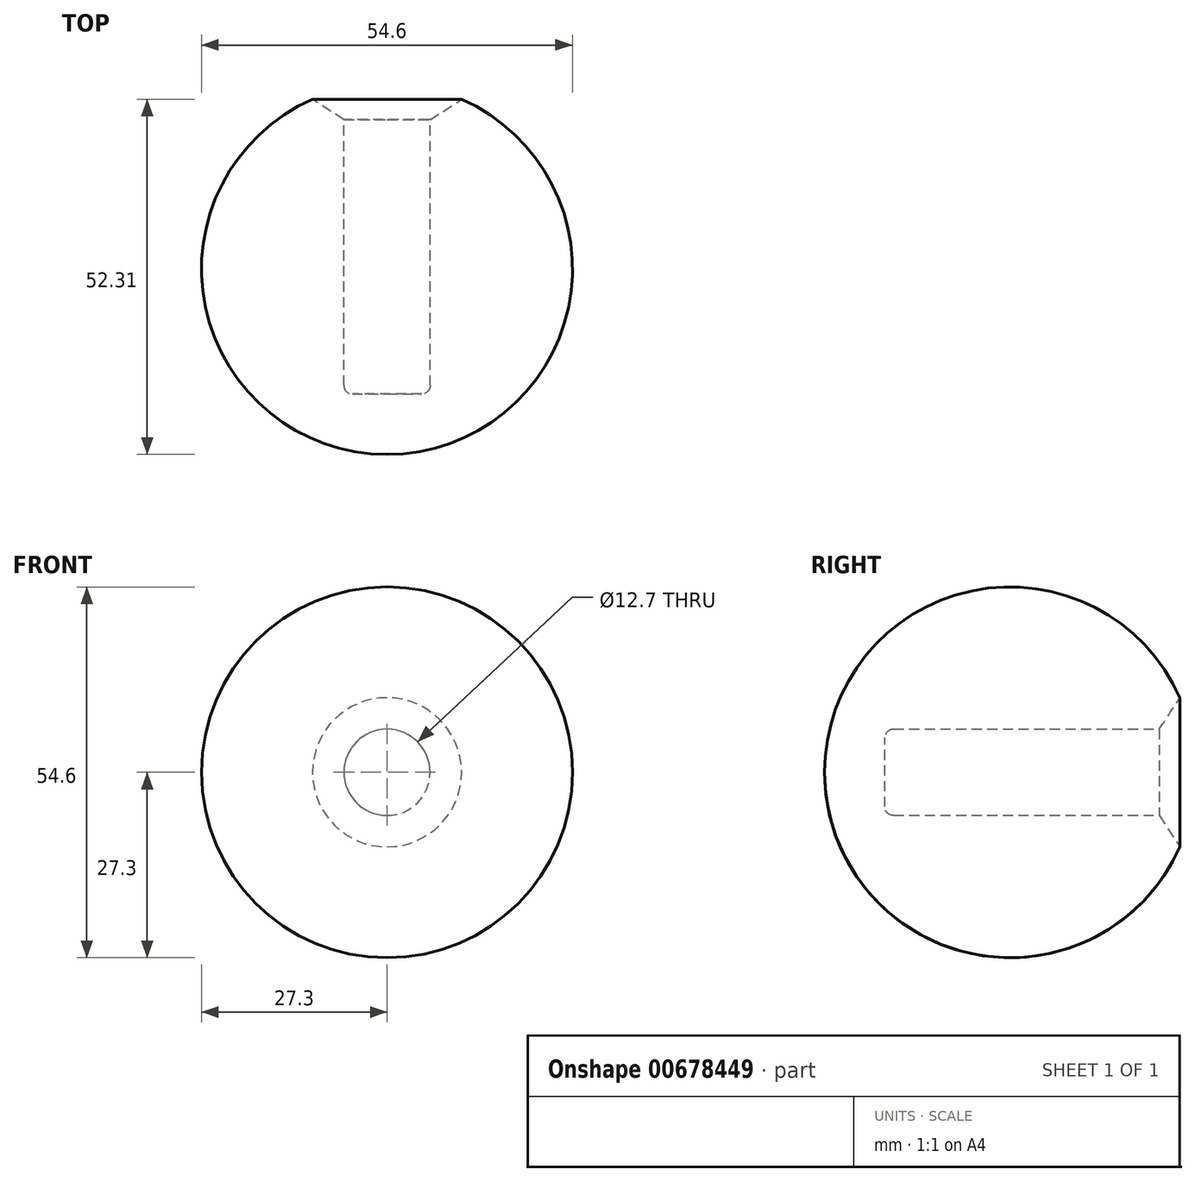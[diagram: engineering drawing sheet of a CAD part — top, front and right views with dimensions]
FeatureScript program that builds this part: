
annotation { "Feature Type Name" : "Feature", "Feature Type Description" : "" }
export const myFeature = defineFeature(function(context is Context, id is Id, definition is map)
    precondition{}
    {
        {
            var Q0;
            Q0=qCreatedBy(makeId("Front.planeOp"),FACE);
            var sketch = newSketch(context, id + "F0", { "sketchPlane" : qUnion([Q0])});
            skCircle(sketch, "E0", {"center": v(0, 0) * mm, "radius": 27.3 * mm});
            skSolve(sketch);
        }
        {
            var Q0;
            Q0 = qSketchRegion(id + "F0", true);
            extrude(context, id + "F1", {"entities" : qUnion([Q0]), "depth" : 54.6 * mm, "offsetDistance" : 25.4 * mm});
        }
        {
            var Q0;
            Q0=makeQuery(id+"F1.opExtrude","CAP_EDGE",EDGE,{"disambiguationData":[OSD([sQuery(id+"F0.wireOp",EDGE,"E0")])],"isStart":false});
            var Q1;
            Q1=makeQuery(id+"F1.opExtrude","CAP_EDGE",EDGE,{"disambiguationData":[OSD([sQuery(id+"F0.wireOp",EDGE,"E0")])],"isStart":true});
            fillet(context, id + "F2", {"entities" : qUnion([Q0, Q1]), "radius" : 27.3 * mm, "tangentPropagation" : true, "allowEdgeOverflow" : false});
        }
        {
            var Q0;
            Q0=qCreatedBy(makeId("Front.planeOp"),FACE);
            var sketch = newSketch(context, id + "F3", { "sketchPlane" : qUnion([Q0])});
            skCircle(sketch, "E1", {"center": v(0, 0) * mm, "radius": 6.35 * mm});
            skSolve(sketch);
        }
        {
            var Q0;
            Q0 = qSketchRegion(id + "F3", true);
            extrude(context, id + "F4", {"entities" : qUnion([Q0]), "operationType" : NewBodyOperationType.REMOVE, "depth" : 45.72 * mm, "offsetDistance" : 25.4 * mm});
        }
        {
            var Q0;
            Q0=makeQuery(id+"F4.boolean.opBoolean","COPY",EDGE,{"derivedFrom":makeQuery(id+"F4.opExtrude","CAP_EDGE",EDGE,{"disambiguationData":[OSD([sQuery(id+"F3.wireOp",EDGE,"E1")])],"isStart":false})});
            fillet(context, id + "F5", {"entities" : qUnion([Q0]), "radius" : 1.27 * mm, "tangentPropagation" : true, "allowEdgeOverflow" : false});
        }
        {
            var Q0;
            Q0=makeQuery(id+"F4.boolean.opBoolean","INTERSECT",EDGE,{"derivedFrom":[makeQuery(id+"F2.opFillet","BLEND_FACE",FACE,{"disambiguationData":[OSD([sQuery(id+"F0.wireOp",EDGE,"E0")])]}),makeQuery(id+"F4.opExtrude","SWEPT_FACE",FACE,{"disambiguationData":[OSD([sQuery(id+"F3.wireOp",EDGE,"E1")])]})]});
            chamfer(context, id + "F6", {"entities" : qUnion([Q0]), "width" : 3.3 * mm, "tangentPropagation" : true});
        }
    });
